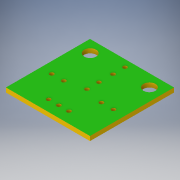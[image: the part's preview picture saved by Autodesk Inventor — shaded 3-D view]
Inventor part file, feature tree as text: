
AUTODESK INVENTOR PART (.ipt)
format: ipt  version: 2016 (Build 200138000, 138)  size: 162,816 bytes
history: native  units: in
note: dims shown in document units (in); Inventor stores cm internally (conversion verified against a paired STEP export)
features: extrude x2, sketch x2
ambient origin geometry x8: Origin, YZ Plane, XZ Plane, XY Plane, X Axis, Y Axis, Z Axis, Center Point
bodies: Solid1 (feature_tree)
feature tree (4):
  extrude  "Extrusion1"  Depth=0.8268in
  extrude  "Extrusion2"  Depth=0.0433in
  sketch  "Sketch1"  dims[d0=0.8268in d1=0.8268in]
  sketch  "Sketch2"  dims[d2=0.0433in d3=0.0in d4=0.1181in d5=0.1181in d10=0.0394in d12=0.0394in d14=0.0394in d15=0.0394in d16=0.0394in d23=0.1in d24=0.1in d25=0.0394in d27=0.0394in d28=0.1181in d31=0.0394in d32=0.0394in d36=0.1181in d37=0.0394in d38=0.0394in d40=0.1181in d43=0.0433in d44=0.0in]
